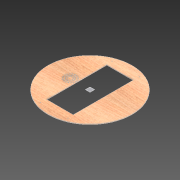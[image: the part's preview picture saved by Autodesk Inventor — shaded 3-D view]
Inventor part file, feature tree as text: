
AUTODESK INVENTOR PART (.ipt)
format: ipt  version: 2020 (Build 240168000, 168)  size: 259,584 bytes
history: native  units: in
note: dims shown in document units (in); Inventor stores cm internally (conversion verified against a paired STEP export)
features: sketch x4, extrude x4, plane x4
ambient origin geometry x8: Origin, YZ Plane, XZ Plane, XY Plane, X Axis, Y Axis, Z Axis, Center Point
bodies: Solid1 (feature_tree)
feature tree (12):
  sketch  "Sketch1"  dims[d0=15.748in d3=5.0in]
  extrude  "Extrusion7"  Depth=5.0in
  plane  "Work Plane1"
  extrude  "Extrusion2"  Depth=0.1181in TaperAngle=0.0deg
  plane  "Work Plane4"
  extrude  "Extrusion3"  Depth=1.1811in
  plane  "Work Plane2"
  extrude  "Extrusion4"  Depth=0.1181in
  plane  "Work Plane3"
  sketch  "Sketch2"  dims[d4=11.2992in d5=0.1181in d6=0.0in]
  sketch  "Sketch3"  dims[d7=2.3622in d8=1.1811in]
  sketch  "Sketch4"  dims[d9=1.0236in d10=0.1969in d11=7.0866in d13=360.0deg d15=0.6693in d16=0.3937in d18=0.1575in d19=0.1181in d20=7.0866in d22=360.0deg d24=3.937in d26=360.0deg d28=0.3937in d29=0.0in d30=6.6929in d31=13.3858in d32=1.5748in d33=0.9843in d34=2.5591in d35=2.5591in d36=2.5591in d37=2.5591in d38=2.5591in d39=0.1181in d40=0.1181in d41=0.1181in d42=0.1181in d43=0.3937in d44=0.0in d55=0.1181in d56=0.0in]
